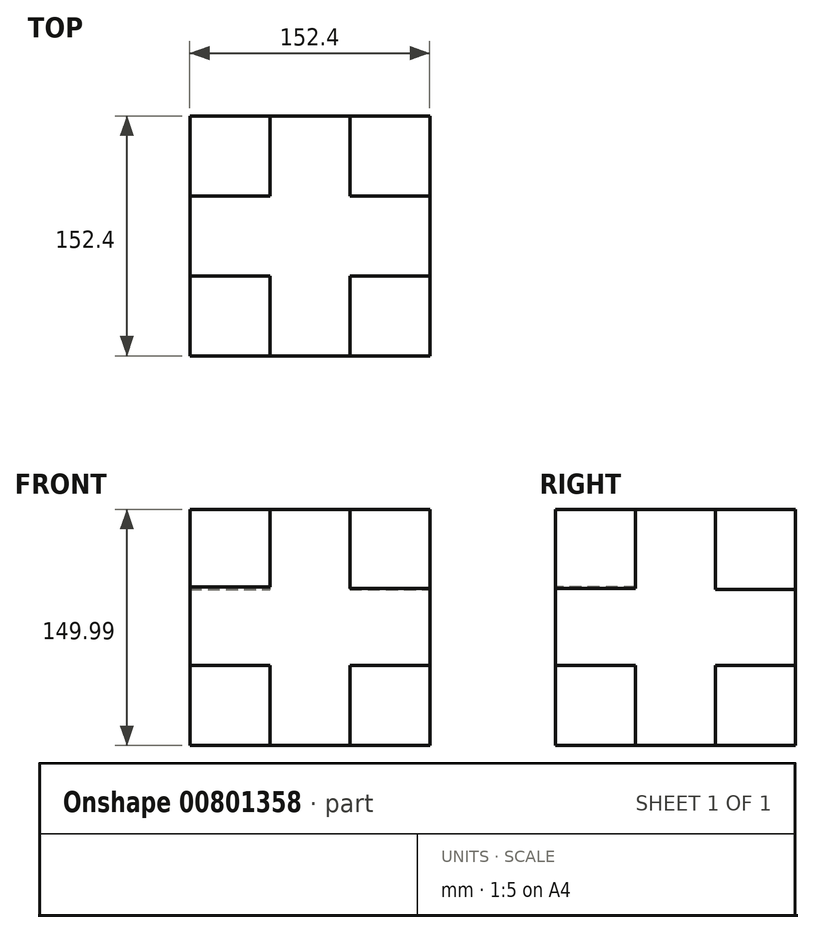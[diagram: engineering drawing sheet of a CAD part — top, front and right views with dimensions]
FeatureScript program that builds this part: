
annotation { "Feature Type Name" : "Feature", "Feature Type Description" : "" }
export const myFeature = defineFeature(function(context is Context, id is Id, definition is map)
    precondition{}
    {
        {
            var Q0;
            Q0=qCreatedBy(makeId("Front.planeOp"),FACE);
            var sketch = newSketch(context, id + "F0", { "sketchPlane" : qUnion([Q0])});
            skLineSegment(sketch, "E0.bottom", {"start": v(-72.75, 78.16) * mm, "end": v(79.65, 78.16) * mm});
            skLineSegment(sketch, "E0.top", {"start": v(-72.75, -71.83) * mm, "end": v(79.65, -71.83) * mm});
            skLineSegment(sketch, "E0.left", {"start": v(-72.75, 78.16) * mm, "end": v(-72.75, -71.83) * mm});
            skLineSegment(sketch, "E0.right", {"start": v(79.65, 78.16) * mm, "end": v(79.65, -71.83) * mm});
            skSolve(sketch);
        }
        {
            var Q0;
            Q0 = qSketchRegion(id + "F0", true);
            var Q1;
            Q1 = qSketchRegion(id + "F8", true);
            extrude(context, id + "F1", {"entities" : qUnion([Q0, Q1]), "depth" : 152.4 * mm, "offsetDistance" : 25.4 * mm});
        }
        {
            var Q0;
            Q0=makeQuery(id+"F1.opExtrude","CAP_FACE",FACE,{"disambiguationData":[OSD([sQuery(id+"F0.wireOp",EDGE,"E0.bottom"),sQuery(id+"F0.wireOp",EDGE,"E0.top"),sQuery(id+"F0.wireOp",EDGE,"E0.left"),sQuery(id+"F0.wireOp",EDGE,"E0.right")])],"isStart":false});
            var sketch = newSketch(context, id + "F2", { "sketchPlane" : qUnion([Q0])});
            skLineSegment(sketch, "E1.bottom", {"start": v(-72.75, 78.16) * mm, "end": v(-21.95, 78.16) * mm});
            skLineSegment(sketch, "E1.top", {"start": v(-72.75, 28.97) * mm, "end": v(-21.95, 28.97) * mm});
            skLineSegment(sketch, "E1.left", {"start": v(-72.75, 78.16) * mm, "end": v(-72.75, 28.97) * mm});
            skLineSegment(sketch, "E1.right", {"start": v(-21.95, 78.16) * mm, "end": v(-21.95, 28.97) * mm});
            skSolve(sketch);
        }
        {
            var Q0;
            Q0=makeQuery(id+"F2.imprint","IMPRINT",FACE,{"disambiguationData":[TD([[makeQuery(id+"F2.imprint","IMPRINT",EDGE,{"derivedFrom":sQuery(id+"F2.wireOp",EDGE,"E1.bottom")}),-1.0]])]});
            extrude(context, id + "F3", {"entities" : qUnion([Q0]), "operationType" : NewBodyOperationType.REMOVE, "oppositeDirection" : true, "depth" : 50.8 * mm, "offsetDistance" : 25.4 * mm});
        }
        {
            var Q0;
            Q0=makeQuery(id+"F1.opExtrude","CAP_FACE",FACE,{"disambiguationData":[OSD([sQuery(id+"F0.wireOp",EDGE,"E0.bottom"),sQuery(id+"F0.wireOp",EDGE,"E0.top"),sQuery(id+"F0.wireOp",EDGE,"E0.left"),sQuery(id+"F0.wireOp",EDGE,"E0.right")])],"isStart":false});
            var sketch = newSketch(context, id + "F4", { "sketchPlane" : qUnion([Q0])});
            skLineSegment(sketch, "E2.bottom", {"start": v(79.65, 78.16) * mm, "end": v(28.85, 78.16) * mm});
            skLineSegment(sketch, "E2.top", {"start": v(79.65, 27.81) * mm, "end": v(28.85, 27.81) * mm});
            skLineSegment(sketch, "E2.left", {"start": v(79.65, 78.16) * mm, "end": v(79.65, 27.81) * mm});
            skLineSegment(sketch, "E2.right", {"start": v(28.85, 78.16) * mm, "end": v(28.85, 27.81) * mm});
            skSolve(sketch);
        }
        {
            var Q0;
            Q0=makeQuery(id+"F4.imprint","IMPRINT",FACE,{"disambiguationData":[TD([[makeQuery(id+"F4.imprint","IMPRINT",EDGE,{"derivedFrom":sQuery(id+"F4.wireOp",EDGE,"E2.bottom")}),-1.0]])]});
            extrude(context, id + "F5", {"entities" : qUnion([Q0]), "operationType" : NewBodyOperationType.REMOVE, "oppositeDirection" : true, "depth" : 50.8 * mm, "offsetDistance" : 25.4 * mm});
        }
        {
            var Q0;
            Q0=makeQuery(id+"F1.opExtrude","CAP_FACE",FACE,{"disambiguationData":[OSD([sQuery(id+"F0.wireOp",EDGE,"E0.bottom"),sQuery(id+"F0.wireOp",EDGE,"E0.top"),sQuery(id+"F0.wireOp",EDGE,"E0.left"),sQuery(id+"F0.wireOp",EDGE,"E0.right")])],"isStart":false});
            var sketch = newSketch(context, id + "F6", { "sketchPlane" : qUnion([Q0])});
            skLineSegment(sketch, "E3.bottom", {"start": v(-72.75, -71.83) * mm, "end": v(-21.95, -71.83) * mm});
            skLineSegment(sketch, "E3.top", {"start": v(-72.75, -21.03) * mm, "end": v(-21.95, -21.03) * mm});
            skLineSegment(sketch, "E3.left", {"start": v(-72.75, -71.83) * mm, "end": v(-72.75, -21.03) * mm});
            skLineSegment(sketch, "E3.right", {"start": v(-21.95, -71.83) * mm, "end": v(-21.95, -21.03) * mm});
            skSolve(sketch);
        }
        {
            var Q0;
            Q0 = qSketchRegion(id + "F6", true);
            var Q1;
            Q1=sQuery(id+"F6.wireOp",EDGE,"E3.right");
            var Q2;
            Q2=sQuery(id+"F6.wireOp",EDGE,"E3.top");
            var Q3;
            Q3=sQuery(id+"F6.wireOp",EDGE,"E3.left");
            var Q4;
            Q4=sQuery(id+"F6.wireOp",EDGE,"E3.bottom");
            extrude(context, id + "F7", {"entities" : qUnion([Q0]), "operationType" : NewBodyOperationType.REMOVE, "surfaceEntities" : qUnion([Q1, Q2, Q3, Q4]), "endBound" : BoundingType.THROUGH_ALL, "depth" : 50.8 * mm, "offsetDistance" : 25.4 * mm});
        }
        {
            var Q0;
            Q0=makeQuery(id+"F1.opExtrude","CAP_FACE",FACE,{"disambiguationData":[OSD([sQuery(id+"F0.wireOp",EDGE,"E0.bottom"),sQuery(id+"F0.wireOp",EDGE,"E0.top"),sQuery(id+"F0.wireOp",EDGE,"E0.left"),sQuery(id+"F0.wireOp",EDGE,"E0.right")])],"isStart":true});
            var sketch = newSketch(context, id + "F8", { "sketchPlane" : qUnion([Q0])});
            skLineSegment(sketch, "E4.bottom", {"start": v(-79.65, -71.83) * mm, "end": v(-28.85, -71.83) * mm});
            skLineSegment(sketch, "E4.top", {"start": v(-79.65, -21.03) * mm, "end": v(-28.85, -21.03) * mm});
            skLineSegment(sketch, "E4.left", {"start": v(-79.65, -71.83) * mm, "end": v(-79.65, -21.03) * mm});
            skLineSegment(sketch, "E4.right", {"start": v(-28.85, -71.83) * mm, "end": v(-28.85, -21.03) * mm});
            skLineSegment(sketch, "E5.bottom", {"start": v(72.75, -71.83) * mm, "end": v(21.95, -71.83) * mm});
            skLineSegment(sketch, "E5.top", {"start": v(72.75, -21.03) * mm, "end": v(21.95, -21.03) * mm});
            skLineSegment(sketch, "E5.left", {"start": v(72.75, -71.83) * mm, "end": v(72.75, -21.03) * mm});
            skLineSegment(sketch, "E5.right", {"start": v(21.95, -71.83) * mm, "end": v(21.95, -21.03) * mm});
            skSolve(sketch);
        }
        {
            var Q0;
            Q0 = qSketchRegion(id + "F8", true);
            extrude(context, id + "F9", {"entities" : qUnion([Q0]), "operationType" : NewBodyOperationType.REMOVE, "oppositeDirection" : true, "depth" : 50.8 * mm, "offsetDistance" : 25.4 * mm});
        }
        {
            var Q0;
            Q0=makeQuery(id+"F1.opExtrude","SWEPT_FACE",FACE,{"disambiguationData":[OSD([sQuery(id+"F0.wireOp",EDGE,"E0.top")])]});
            var sketch = newSketch(context, id + "F10", { "sketchPlane" : qUnion([Q0])});
            skLineSegment(sketch, "E6.bottom", {"start": v(-72.75, 152.4) * mm, "end": v(-21.95, 152.4) * mm});
            skLineSegment(sketch, "E6.top", {"start": v(-72.75, 101.6) * mm, "end": v(-21.95, 101.6) * mm});
            skLineSegment(sketch, "E6.left", {"start": v(-72.75, 152.4) * mm, "end": v(-72.75, 101.6) * mm});
            skLineSegment(sketch, "E6.right", {"start": v(-21.95, 152.4) * mm, "end": v(-21.95, 101.6) * mm});
            skLineSegment(sketch, "E7.bottom", {"start": v(79.65, 152.4) * mm, "end": v(28.85, 152.4) * mm});
            skLineSegment(sketch, "E7.top", {"start": v(79.65, 101.6) * mm, "end": v(28.85, 101.6) * mm});
            skLineSegment(sketch, "E7.left", {"start": v(79.65, 152.4) * mm, "end": v(79.65, 101.6) * mm});
            skLineSegment(sketch, "E7.right", {"start": v(28.85, 152.4) * mm, "end": v(28.85, 101.6) * mm});
            skSolve(sketch);
        }
        {
            var Q0;
            Q0 = qSketchRegion(id + "F10", true);
            extrude(context, id + "F11", {"entities" : qUnion([Q0]), "operationType" : NewBodyOperationType.REMOVE, "oppositeDirection" : true, "depth" : 50.8 * mm, "offsetDistance" : 25.4 * mm});
        }
        {
            var Q0;
            Q0=makeQuery(id+"F1.opExtrude","SWEPT_FACE",FACE,{"disambiguationData":[OSD([sQuery(id+"F0.wireOp",EDGE,"E0.bottom")])]});
            var sketch = newSketch(context, id + "F12", { "sketchPlane" : qUnion([Q0])});
            skLineSegment(sketch, "E8.bottom", {"start": v(-72.75, 0) * mm, "end": v(-21.95, 0) * mm});
            skLineSegment(sketch, "E8.top", {"start": v(-72.75, -50.8) * mm, "end": v(-21.95, -50.8) * mm});
            skLineSegment(sketch, "E8.left", {"start": v(-72.75, 0) * mm, "end": v(-72.75, -50.8) * mm});
            skLineSegment(sketch, "E8.right", {"start": v(-21.95, 0) * mm, "end": v(-21.95, -50.8) * mm});
            skLineSegment(sketch, "E9.bottom", {"start": v(79.65, 0) * mm, "end": v(28.85, 0) * mm});
            skLineSegment(sketch, "E9.top", {"start": v(79.65, -50.8) * mm, "end": v(28.85, -50.8) * mm});
            skLineSegment(sketch, "E9.left", {"start": v(79.65, 0) * mm, "end": v(79.65, -50.8) * mm});
            skLineSegment(sketch, "E9.right", {"start": v(28.85, 0) * mm, "end": v(28.85, -50.8) * mm});
            skSolve(sketch);
        }
        {
            var Q0;
            Q0 = qSketchRegion(id + "F12", true);
            extrude(context, id + "F13", {"entities" : qUnion([Q0]), "operationType" : NewBodyOperationType.REMOVE, "oppositeDirection" : true, "depth" : 50.8 * mm, "offsetDistance" : 25.4 * mm});
        }
    });
